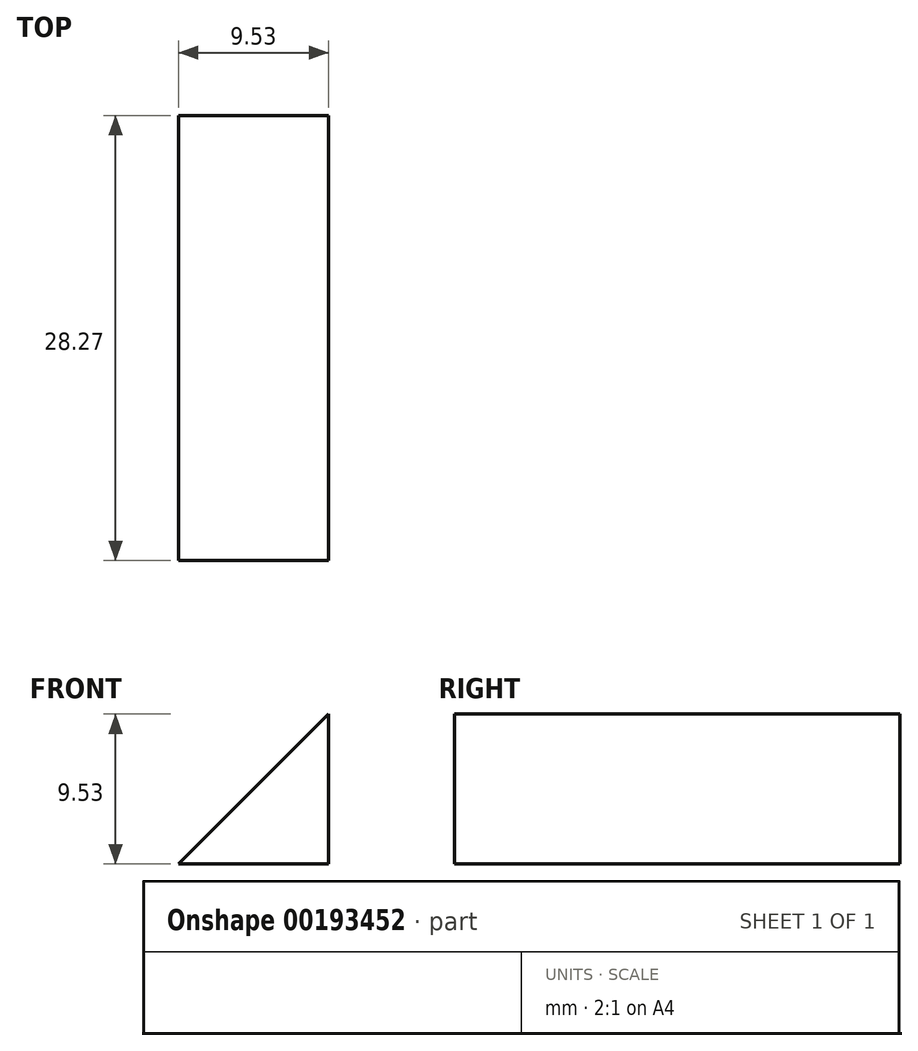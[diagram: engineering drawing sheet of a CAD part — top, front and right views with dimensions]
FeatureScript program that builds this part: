
annotation { "Feature Type Name" : "Feature", "Feature Type Description" : "" }
export const myFeature = defineFeature(function(context is Context, id is Id, definition is map)
    precondition{}
    {
        {
            var Q0;
            Q0=qCreatedBy(makeId("Front.planeOp"),FACE);
            var sketch = newSketch(context, id + "F0", { "sketchPlane" : qUnion([Q0])});
            skLineSegment(sketch, "E0", {"start": v(0, 0) * mm, "end": v(-9.53, 0) * mm});
            skLineSegment(sketch, "E1", {"start": v(0, 0) * mm, "end": v(0, 9.53) * mm});
            skLineSegment(sketch, "E2", {"start": v(0, 9.53) * mm, "end": v(-9.53, 0) * mm});
            skSolve(sketch);
        }
        {
            var Q0;
            Q0=makeQuery(id+"F0.imprint","IMPRINT",FACE,{"disambiguationData":[TD([[makeQuery(id+"F0.imprint","IMPRINT",EDGE,{"derivedFrom":sQuery(id+"F0.wireOp",EDGE,"E0")}),-1.0]])]});
            extrude(context, id + "F1", {"entities" : qUnion([Q0]), "depth" : 28.27 * mm});
        }
    });
